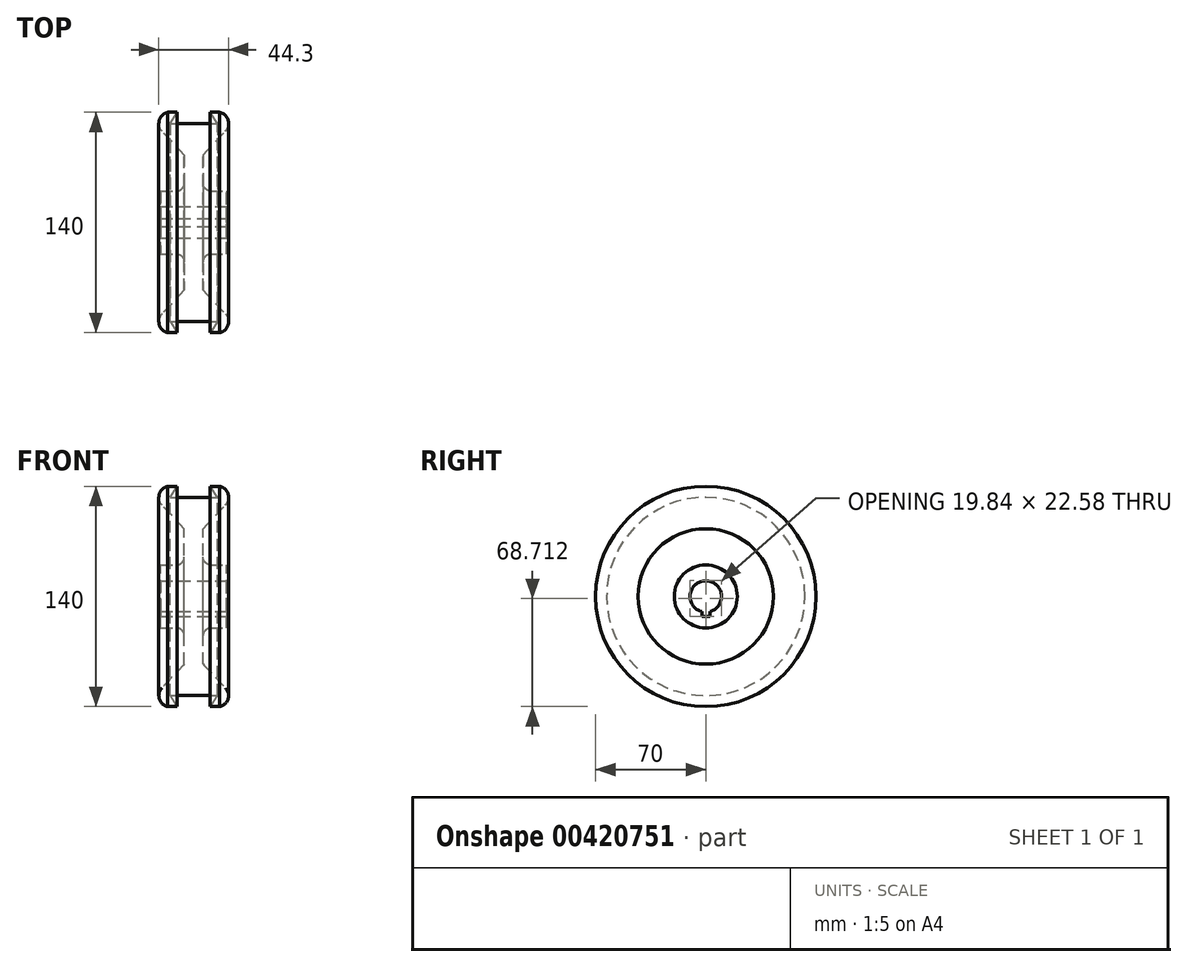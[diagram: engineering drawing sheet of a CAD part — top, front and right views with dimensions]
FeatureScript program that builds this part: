
annotation { "Feature Type Name" : "Feature", "Feature Type Description" : "" }
export const myFeature = defineFeature(function(context is Context, id is Id, definition is map)
    precondition{}
    {
        {
            var Q0;
            Q0=qCreatedBy(makeId("Front.planeOp"),FACE);
            var sketch = newSketch(context, id + "F0", { "sketchPlane" : qUnion([Q0])});
            skLineSegment(sketch, "E0.bottom", {"start": v(0, 0) * mm, "end": v(-42, 0) * mm});
            skLineSegment(sketch, "E1", {"start": v(-42, -10) * mm, "end": v(0, -10) * mm});
            skPoint(sketch, "E2", {"position": v(-42, -20) * mm});
            skPoint(sketch, "E3", {"position": v(0, -20) * mm});
            skLineSegment(sketch, "E4", {"start": v(-42, -20) * mm, "end": v(-32, -20) * mm});
            skLineSegment(sketch, "E5", {"start": v(0, -20) * mm, "end": v(-10, -20) * mm});
            skLineSegment(sketch, "E6", {"start": v(-27, -25) * mm, "end": v(-27, -43) * mm});
            skLineSegment(sketch, "E7", {"start": v(-15, -25) * mm, "end": v(-15, -43) * mm});
            skLineSegment(sketch, "E8", {"start": v(-41.2, -58.1) * mm, "end": v(-27, -43) * mm});
            skLineSegment(sketch, "E9", {"start": v(-15, -43) * mm, "end": v(-0.8, -58.1) * mm});
            skLineSegment(sketch, "E10", {"start": v(-42, -10) * mm, "end": v(-42, -20) * mm});
            skLineSegment(sketch, "E11", {"start": v(0, -20) * mm, "end": v(0, -10) * mm});
            skLineSegment(sketch, "E12", {"start": v(-21, 0) * mm, "end": v(-21, -70) * mm, "construction": true});
            skPoint(sketch, "E13", {"position": v(-10.5, -70) * mm});
            skPoint(sketch, "E14", {"position": v(-31.5, -70) * mm});
            skPoint(sketch, "E15", {"position": v(-36, -63) * mm});
            skPoint(sketch, "E16", {"position": v(-6, -63) * mm});
            skLineSegment(sketch, "E17", {"start": v(-37.47, -70) * mm, "end": v(-31.5, -70) * mm});
            skLineSegment(sketch, "E18", {"start": v(-10.5, -70) * mm, "end": v(-6, -63) * mm});
            skLineSegment(sketch, "E19", {"start": v(-6, -63) * mm, "end": v(-36, -63) * mm});
            skLineSegment(sketch, "E20", {"start": v(-10.5, -70) * mm, "end": v(-4.53, -70) * mm});
            skLineSegment(sketch, "E21", {"start": v(-36, -63) * mm, "end": v(-31.5, -70) * mm});
            skPoint(sketch, "E22.visualSharp", {"position": v(-27, -20) * mm});
            skArc(sketch, "E22.filletArc", {"start": v(-27, -25) * mm, "mid": v(-28.46, -21.46) * mm, "end": v(-32, -20) * mm});
            skPoint(sketch, "E23.visualSharp", {"position": v(-15, -20) * mm});
            skArc(sketch, "E23.filletArc", {"start": v(-10, -20) * mm, "mid": v(-13.54, -21.46) * mm, "end": v(-15, -25) * mm});
            skArc(sketch, "E24", {"start": v(-4.53, -70) * mm, "mid": v(0.83, -65.14) * mm, "end": v(-0.8, -58.1) * mm});
            skArc(sketch, "E25.MirrorCS", {"start": v(-37.47, -70) * mm, "mid": v(-42.83, -65.14) * mm, "end": v(-41.2, -58.1) * mm});
            skSolve(sketch);
        }
        {
            var Q0;
            Q0=makeQuery(id+"F0.imprint","IMPRINT",FACE,{"disambiguationData":[TD([[makeQuery(id+"F0.imprint","IMPRINT",EDGE,{"derivedFrom":sQuery(id+"F0.wireOp",EDGE,"E1")}),-1.0]])]});
            var Q1;
            Q1=sQuery(id+"F0.wireOp",EDGE,"E0.bottom");
            revolve(context, id + "F1", {"entities" : qUnion([Q0]), "axis" : qUnion([Q1]), "revolveType" : RevolveType.FULL});
        }
        {
            var Q0;
            Q0=qCreatedBy(makeId("Right.planeOp"),FACE);
            var sketch = newSketch(context, id + "F2", { "sketchPlane" : qUnion([Q0])});
            skLineSegment(sketch, "E26.bottom", {"start": v(2.5, -9.58) * mm, "end": v(-2.5, -9.58) * mm});
            skLineSegment(sketch, "E26.top", {"start": v(2.5, -12.58) * mm, "end": v(-2.5, -12.58) * mm});
            skLineSegment(sketch, "E26.left", {"start": v(2.5, -9.58) * mm, "end": v(2.5, -12.58) * mm});
            skLineSegment(sketch, "E26.right", {"start": v(-2.5, -9.58) * mm, "end": v(-2.5, -12.58) * mm});
            skSolve(sketch);
        }
        {
            var Q0;
            Q0=makeQuery(id+"F2.imprint","IMPRINT",FACE,{"disambiguationData":[TD([[makeQuery(id+"F2.imprint","IMPRINT",EDGE,{"derivedFrom":sQuery(id+"F2.wireOp",EDGE,"E26.bottom")}),1.0]])]});
            extrude(context, id + "F3", {"entities" : qUnion([Q0]), "operationType" : NewBodyOperationType.REMOVE, "oppositeDirection" : true, "depth" : 53.1 * mm});
        }
    });
